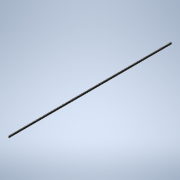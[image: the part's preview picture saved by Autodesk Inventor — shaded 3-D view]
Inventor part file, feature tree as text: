
AUTODESK INVENTOR PART (.ipt)
format: ipt  version: 2022.2 (Build 262287010, 287A)  size: 96,768 bytes
history: native  units: mm
features: extrude x1, sketch x1
ambient origin geometry x8: Origin, YZ Plane, XZ Plane, XY Plane, X Axis, Y Axis, Z Axis, Center Point
bodies: Volumenkörper1 (feature_tree)
feature tree (2):
  extrude  "Extrusion1"  Depth=490.0mm
  sketch  "Skizze1"  dims[d0=1.5mm d1=490.0mm d2=6.0mm d3=0.0mm]
